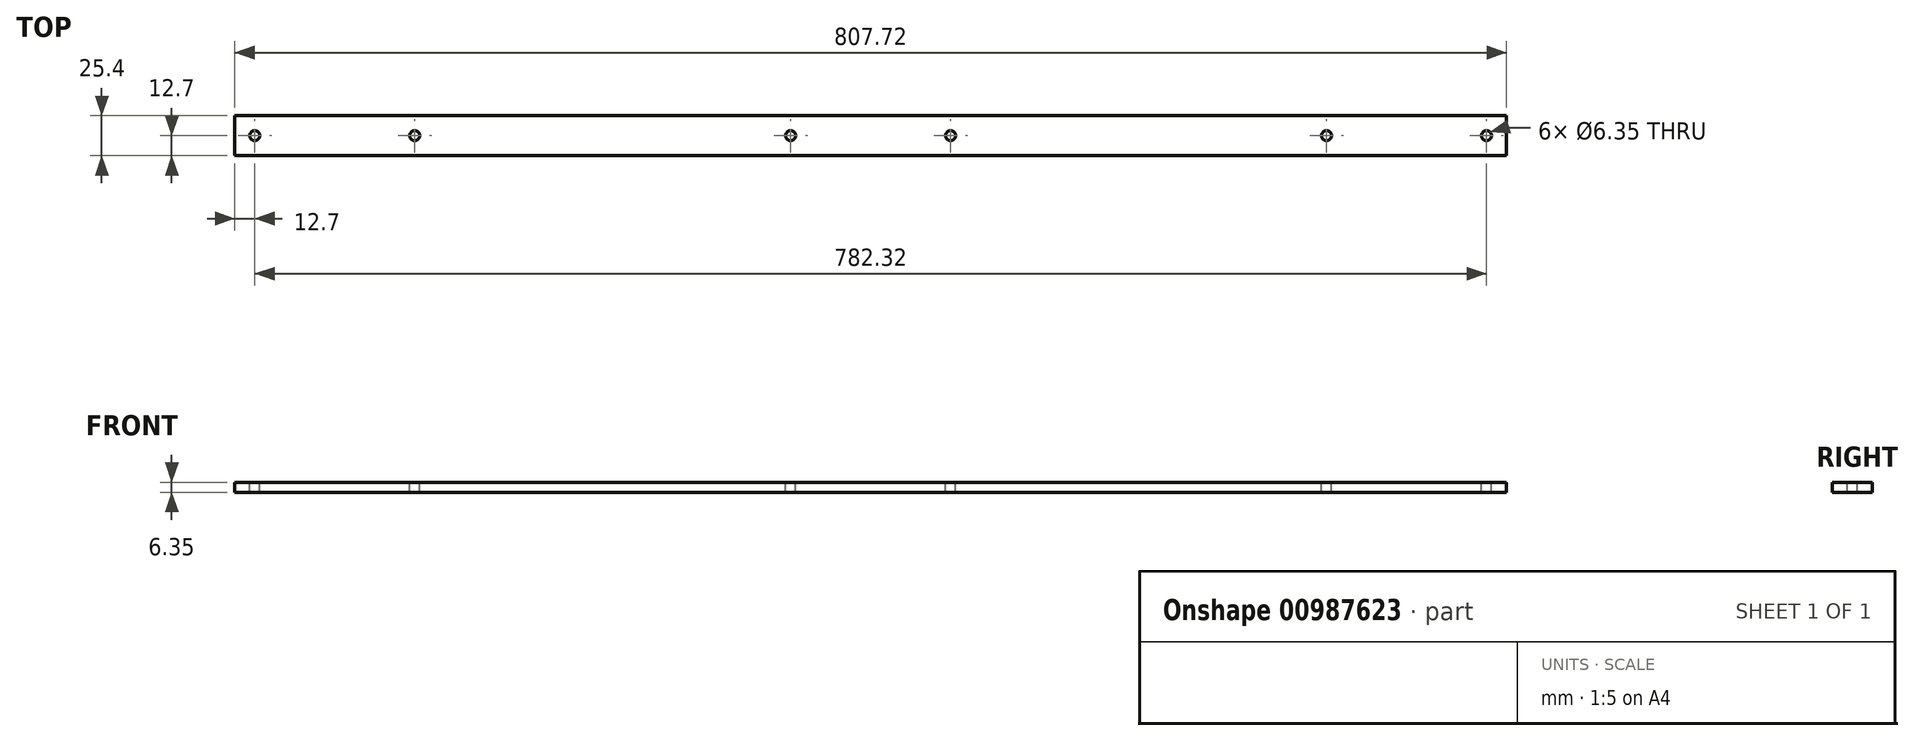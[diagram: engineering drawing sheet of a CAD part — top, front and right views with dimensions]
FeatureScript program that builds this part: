
annotation { "Feature Type Name" : "Feature", "Feature Type Description" : "" }
export const myFeature = defineFeature(function(context is Context, id is Id, definition is map)
    precondition{}
    {
        {
            var Q0;
            Q0=qCreatedBy(makeId("Top.planeOp"),FACE);
            var sketch = newSketch(context, id + "F0", { "sketchPlane" : qUnion([Q0])});
            skLineSegment(sketch, "E0.bottom", {"start": v(403.86, 12.7) * mm, "end": v(-403.86, 12.7) * mm});
            skLineSegment(sketch, "E0.top", {"start": v(403.86, -12.7) * mm, "end": v(-403.86, -12.7) * mm});
            skLineSegment(sketch, "E0.left", {"start": v(403.86, 12.7) * mm, "end": v(403.86, -12.7) * mm});
            skLineSegment(sketch, "E0.right", {"start": v(-403.86, 12.7) * mm, "end": v(-403.86, -12.7) * mm});
            skPoint(sketch, "E0.middle", {"position": v(0, 0) * mm});
            skSolve(sketch);
        }
        {
            var Q0;
            Q0=makeQuery(id+"F0.imprint","IMPRINT",FACE,{"disambiguationData":[TD([[makeQuery(id+"F0.imprint","IMPRINT",EDGE,{"derivedFrom":sQuery(id+"F0.wireOp",EDGE,"E0.bottom")}),1.0]])]});
            extrude(context, id + "F1", {"entities" : qUnion([Q0]), "depth" : 6.35 * mm, "offsetDistance" : 25.4 * mm});
        }
        {
            var Q0;
            Q0=makeQuery(id+"F1.opExtrude","CAP_FACE",FACE,{"disambiguationData":[OSD([sQuery(id+"F0.wireOp",EDGE,"E0.bottom"),sQuery(id+"F0.wireOp",EDGE,"E0.top"),sQuery(id+"F0.wireOp",EDGE,"E0.left"),sQuery(id+"F0.wireOp",EDGE,"E0.right")])],"isStart":false});
            var sketch = newSketch(context, id + "F2", { "sketchPlane" : qUnion([Q0])});
            skCircle(sketch, "E1", {"center": v(-391.16, 0) * mm, "radius": 3.18 * mm});
            skCircle(sketch, "E2", {"center": v(-289.56, 0) * mm, "radius": 3.18 * mm});
            skCircle(sketch, "E3", {"center": v(-50.8, 0) * mm, "radius": 3.18 * mm});
            skCircle(sketch, "E4", {"center": v(50.8, 0) * mm, "radius": 3.18 * mm});
            skCircle(sketch, "E5", {"center": v(289.56, 0) * mm, "radius": 3.18 * mm});
            skCircle(sketch, "E6", {"center": v(391.16, 0) * mm, "radius": 3.18 * mm});
            skSolve(sketch);
        }
        {
            var Q0;
            Q0=makeQuery(id+"F2.imprint","IMPRINT",FACE,{"disambiguationData":[TD([[makeQuery(id+"F2.imprint","IMPRINT",EDGE,{"derivedFrom":sQuery(id+"F2.wireOp",EDGE,"E1")}),1.0]])]});
            var Q1;
            Q1=makeQuery(id+"F2.imprint","IMPRINT",FACE,{"disambiguationData":[TD([[makeQuery(id+"F2.imprint","IMPRINT",EDGE,{"derivedFrom":sQuery(id+"F2.wireOp",EDGE,"E2")}),1.0]])]});
            var Q2;
            Q2=makeQuery(id+"F2.imprint","IMPRINT",FACE,{"disambiguationData":[TD([[makeQuery(id+"F2.imprint","IMPRINT",EDGE,{"derivedFrom":sQuery(id+"F2.wireOp",EDGE,"E3")}),1.0]])]});
            var Q3;
            Q3=makeQuery(id+"F2.imprint","IMPRINT",FACE,{"disambiguationData":[TD([[makeQuery(id+"F2.imprint","IMPRINT",EDGE,{"derivedFrom":sQuery(id+"F2.wireOp",EDGE,"E4")}),1.0]])]});
            var Q4;
            Q4=makeQuery(id+"F2.imprint","IMPRINT",FACE,{"disambiguationData":[TD([[makeQuery(id+"F2.imprint","IMPRINT",EDGE,{"derivedFrom":sQuery(id+"F2.wireOp",EDGE,"E5")}),1.0]])]});
            var Q5;
            Q5=makeQuery(id+"F2.imprint","IMPRINT",FACE,{"disambiguationData":[TD([[makeQuery(id+"F2.imprint","IMPRINT",EDGE,{"derivedFrom":sQuery(id+"F2.wireOp",EDGE,"E6")}),1.0]])]});
            extrude(context, id + "F3", {"entities" : qUnion([Q0, Q1, Q2, Q3, Q4, Q5]), "operationType" : NewBodyOperationType.REMOVE, "oppositeDirection" : true, "depth" : 25.4 * mm, "offsetDistance" : 25.4 * mm});
        }
    });
